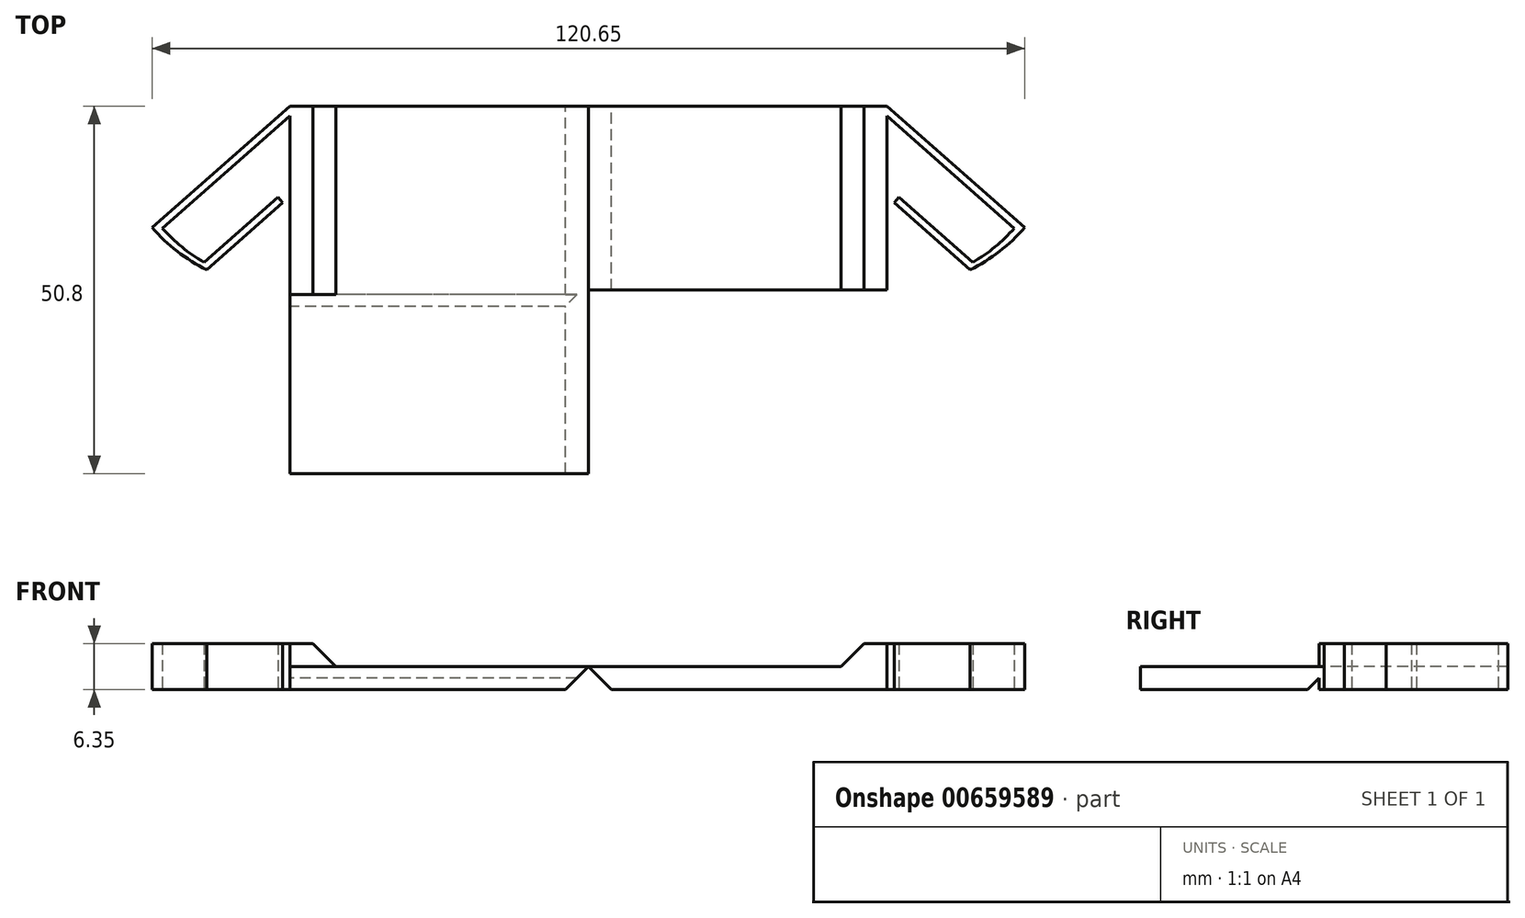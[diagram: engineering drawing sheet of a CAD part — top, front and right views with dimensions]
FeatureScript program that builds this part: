
annotation { "Feature Type Name" : "Feature", "Feature Type Description" : "" }
export const myFeature = defineFeature(function(context is Context, id is Id, definition is map)
    precondition{}
    {
        {
            var Q0;
            Q0=qCreatedBy(makeId("Top.planeOp"),FACE);
            var sketch = newSketch(context, id + "F0", { "sketchPlane" : qUnion([Q0])});
            skLineSegment(sketch, "E0.bottom", {"start": v(28.58, -12.7) * mm, "end": v(-28.58, -12.7) * mm});
            skLineSegment(sketch, "E0.top", {"start": v(28.58, 12.7) * mm, "end": v(-28.58, 12.7) * mm});
            skLineSegment(sketch, "E0.left", {"start": v(28.58, -12.7) * mm, "end": v(28.58, 12.7) * mm});
            skLineSegment(sketch, "E0.right", {"start": v(-28.57, -12.7) * mm, "end": v(-28.57, 12.7) * mm});
            skPoint(sketch, "E0.middle", {"position": v(0, 0) * mm});
            skLineSegment(sketch, "E1", {"start": v(-9.53, 11.37) * mm, "end": v(-9.52, -12.7) * mm});
            skLineSegment(sketch, "E2", {"start": v(0, -12.7) * mm, "end": v(0, 12.7) * mm});
            skPoint(sketch, "E3", {"position": v(-22.22, -12.7) * mm});
            skLineSegment(sketch, "E4", {"start": v(-9.53, 12.7) * mm, "end": v(-28.57, -4.1) * mm});
            skPoint(sketch, "E5", {"position": v(-19.05, -12.7) * mm});
            skArc(sketch, "E6", {"start": v(-28.57, -4.1) * mm, "mid": v(-25.09, -7.37) * mm, "end": v(-21.05, -9.94) * mm});
            skLineSegment(sketch, "E7", {"start": v(-21.05, -9.94) * mm, "end": v(-10.53, -0.66) * mm});
            skLineSegment(sketch, "E8", {"start": v(-10.53, -0.66) * mm, "end": v(-11.19, 0.1) * mm});
            skLineSegment(sketch, "E9", {"start": v(-11.19, 0.1) * mm, "end": v(-11.19, 0.1) * mm});
            skLineSegment(sketch, "E10", {"start": v(-9.53, 11.37) * mm, "end": v(-27.15, -4.18) * mm});
            skArc(sketch, "E11", {"start": v(-27.15, -4.18) * mm, "mid": v(-24.46, -6.77) * mm, "end": v(-21.4, -8.91) * mm});
            skLineSegment(sketch, "E12", {"start": v(-21.4, -8.91) * mm, "end": v(-11.19, 0.1) * mm});
            skSolve(sketch);
        }
        {
            var Q0;
            {var subQ0=sQuery(id+"F0.wireOp",EDGE,"E0.left");Q0=makeQuery(id+"F0.imprint","IMPRINT",FACE,{"disambiguationData":[TD([[makeQuery(id+"F0.imprint","IMPRINT",EDGE,{"derivedFrom":subQ0}),1.0]])]});}
            var Q1;
            {var subQ1=sQuery(id+"F0.wireOp",EDGE,"E1");Q1=makeQuery(id+"F0.imprint","IMPRINT",FACE,{"disambiguationData":[TD([[makeQuery(id+"F0.imprint","IMPRINT",EDGE,{"derivedFrom":subQ1}),1.0]])]});}
            var Q2;
            {var subQ0=sQuery(id+"F0.wireOp",EDGE,"Ll8NUgnO-918t-zldm-zNWz-RsUZQomu35K8");Q2=makeQuery(id+"F0.imprint","IMPRINT",FACE,{"disambiguationData":[TD([[makeQuery(id+"F0.imprint","IMPRINT",EDGE,{"derivedFrom":subQ0}),1.0]])]});}
            extrude(context, id + "F1", {"entities" : qUnion([Q0, Q1, Q2]), "depth" : 3.17 * mm, "offsetDistance" : 25.4 * mm});
        }
        {
            var Q0;
            {var subQ1=sQuery(id+"F0.wireOp",EDGE,"E1");Q0=makeQuery(id+"F0.imprint","IMPRINT",FACE,{"disambiguationData":[TD([[makeQuery(id+"F0.imprint","IMPRINT",EDGE,{"derivedFrom":subQ1}),1.0]])]});}
            extrude(context, id + "F2", {"entities" : qUnion([Q0]), "operationType" : NewBodyOperationType.ADD, "depth" : 6.35 * mm, "offsetDistance" : 25.4 * mm});
        }
        {
            var Q0;
            Q0=makeQuery(id+"F2.opExtrude","CAP_EDGE",EDGE,{"disambiguationData":[OSD([sQuery(id+"F0.wireOp",EDGE,"E2")])],"isStart":false});
            chamfer(context, id + "F3", {"entities" : qUnion([Q0]), "width" : 6.35 * mm, "tangentPropagation" : true});
        }
        {
            var Q0;
            {var subQ0=sQuery(id+"F0.wireOp",EDGE,"E0.left");Q0=makeQuery(id+"F37SAEC6IVc2ddh_1.boolean.opBoolean","MERGE",FACE,{"derivedFrom":[makeQuery(id+"F1.opExtrude","SWEPT_FACE",FACE,{"disambiguationData":[OSD([subQ0])]}),makeQuery(id+"F37SAEC6IVc2ddh_1.opExtrude","SWEPT_FACE",FACE,{"disambiguationData":[OSD([subQ0])]})]});}
            cPlane(context, id + "F4", {"entities" : qUnion([Q0]), "cplaneType" : CPlaneType.OFFSET, "offset" : 3.17 * mm, "width" : 152.4 * mm, "height" : 152.4 * mm});
        }
        {
            var Q0;
            Q0=makeQuery(id+"F1.opExtrude","SWEPT_BODY",BODY,{"disambiguationData":[OSD([sQuery(id+"F0.wireOp",EDGE,"E0.bottom"),sQuery(id+"F0.wireOp",EDGE,"E0.top"),sQuery(id+"F0.wireOp",EDGE,"E0.left"),sQuery(id+"F0.wireOp",EDGE,"E1"),sQuery(id+"F0.wireOp",EDGE,"E4"),sQuery(id+"F0.wireOp",EDGE,"E6"),sQuery(id+"F0.wireOp",EDGE,"E7"),sQuery(id+"F0.wireOp",EDGE,"E8"),sQuery(id+"F0.wireOp",EDGE,"E10"),sQuery(id+"F0.wireOp",EDGE,"E11"),sQuery(id+"F0.wireOp",EDGE,"E12")])]});
            var Q1;
            Q1=qCreatedBy(id+"F4.planeOp",FACE);
            mirror(context, id + "F5", {"entities" : qUnion([Q0]), "mirrorPlane" : qUnion([Q1])});
        }
        {
            var Q0;
            {var subQ0=sQuery(id+"F0.wireOp",EDGE,"E0.bottom");Q0=makeQuery(id+"F2.boolean.opBoolean","MERGE",FACE,{"derivedFrom":[makeQuery(id+"F1.opExtrude","SWEPT_FACE",FACE,{"disambiguationData":[OSD([subQ0])]}),makeQuery(id+"F2.opExtrude","SWEPT_FACE",FACE,{"disambiguationData":[OSD([subQ0])]})]});}
            var sketch = newSketch(context, id + "F6", { "sketchPlane" : qUnion([Q0])});
            skLineSegment(sketch, "E13", {"start": v(28.57, 3.18) * mm, "end": v(31.75, 3.18) * mm});
            skLineSegment(sketch, "E14", {"start": v(31.75, 3.17) * mm, "end": v(28.57, 0) * mm});
            skLineSegment(sketch, "E15", {"start": v(28.57, 0) * mm, "end": v(28.57, 3.18) * mm});
            skLineSegment(sketch, "E16", {"start": v(31.75, 3.18) * mm, "end": v(34.92, 3.18) * mm});
            skLineSegment(sketch, "E17", {"start": v(34.92, 0) * mm, "end": v(31.75, 3.18) * mm});
            skLineSegment(sketch, "E18", {"start": v(34.92, 0) * mm, "end": v(34.92, 3.18) * mm});
            skSolve(sketch);
        }
        {
            var Q0;
            Q0=makeQuery(id+"F6.imprint","IMPRINT",FACE,{"disambiguationData":[TD([[makeQuery(id+"F6.imprint","IMPRINT",EDGE,{"derivedFrom":sQuery(id+"F6.wireOp",EDGE,"E16")}),-1.0]])]});
            var Q1;
            Q1=makeQuery(id+"F6.imprint","IMPRINT",FACE,{"disambiguationData":[TD([[makeQuery(id+"F6.imprint","IMPRINT",EDGE,{"derivedFrom":sQuery(id+"F6.wireOp",EDGE,"E13")}),-1.0]])]});
            var Q2;
            {var subQ0=sQuery(id+"F0.wireOp",EDGE,"E0.bottom");Q2=makeQuery(id+"F5.opPattern","COPY",FACE,{"derivedFrom":makeQuery(id+"F2.boolean.opBoolean","MERGE",FACE,{"derivedFrom":[makeQuery(id+"F1.opExtrude","SWEPT_FACE",FACE,{"disambiguationData":[OSD([subQ0])]}),makeQuery(id+"F2.opExtrude","SWEPT_FACE",FACE,{"disambiguationData":[OSD([subQ0])]})]}),"instanceName":"1"});}
            var Q3;
            Q3=makeQuery(id+"F6.imprint","IMPRINT",FACE,{"disambiguationData":[TD([[makeQuery(id+"F6.imprint","IMPRINT",EDGE,{"derivedFrom":sQuery(id+"F6.wireOp",EDGE,"E15")}),-1.0]])]});
            extrude(context, id + "F7", {"entities" : qUnion([Q0, Q1, Q2, Q3]), "operationType" : NewBodyOperationType.ADD, "oppositeDirection" : true, "depth" : 25.4 * mm, "offsetDistance" : 25.4 * mm});
        }
        {
            var Q0;
            {var subQ0=sQuery(id+"F0.wireOp",EDGE,"E0.bottom");Q0=makeQuery(id+"F7.boolean.opBoolean","MERGE",FACE,{"derivedFrom":[makeQuery(id+"F2.boolean.opBoolean","MERGE",FACE,{"derivedFrom":[makeQuery(id+"F1.opExtrude","SWEPT_FACE",FACE,{"disambiguationData":[OSD([subQ0])]}),makeQuery(id+"F2.opExtrude","SWEPT_FACE",FACE,{"disambiguationData":[OSD([subQ0])]})]}),makeQuery(id+"F7.opExtrude","CAP_FACE",FACE,{"disambiguationData":[OSD([subQ0,sQuery(id+"F0.wireOp",EDGE,"E1"),sQuery(id+"F0.wireOp",EDGE,"E2"),sQuery(id+"F6.wireOp",EDGE,"E13"),sQuery(id+"F6.wireOp",EDGE,"E14")])],"isStart":true})]});}
            extrude(context, id + "F8", {"entities" : qUnion([Q0]), "operationType" : NewBodyOperationType.ADD, "depth" : 25.4 * mm, "offsetDistance" : 25.4 * mm});
        }
        {
            var Q0;
            {var subQ0=sQuery(id+"F0.wireOp",EDGE,"E1");Q0=makeQuery(id+"F8.boolean.opBoolean","MERGE",FACE,{"derivedFrom":[makeQuery(id+"F2.boolean.opBoolean","MERGE",FACE,{"derivedFrom":[makeQuery(id+"F1.opExtrude","SWEPT_FACE",FACE,{"disambiguationData":[OSD([subQ0])]}),makeQuery(id+"F2.opExtrude","SWEPT_FACE",FACE,{"disambiguationData":[OSD([subQ0])]})]}),makeQuery(id+"F8.opExtrude","SWEPT_FACE",FACE,{"disambiguationData":[OSD([sQuery(id+"F0.wireOp",EDGE,"E0.bottom"),subQ0])]})]});}
            var sketch = newSketch(context, id + "F9", { "sketchPlane" : qUnion([Q0])});
            skPoint(sketch, "E19.oppositeSnap0", {"position": v(13.37, 0) * mm});
            skPoint(sketch, "E19.oppositeSnap1", {"position": v(38.1, 3.18) * mm});
            skLineSegment(sketch, "E19.bottom", {"start": v(38.1, 6.35) * mm, "end": v(13.37, 6.35) * mm});
            skLineSegment(sketch, "E19.top", {"start": v(38.1, 3.18) * mm, "end": v(13.37, 3.18) * mm});
            skLineSegment(sketch, "E19.left", {"start": v(38.1, 6.35) * mm, "end": v(38.1, 3.18) * mm});
            skLineSegment(sketch, "E19.right", {"start": v(13.37, 6.35) * mm, "end": v(13.37, 3.18) * mm});
            skSolve(sketch);
        }
        {
            var Q0;
            Q0 = qSketchRegion(id + "F9", true);
            extrude(context, id + "F10", {"entities" : qUnion([Q0]), "operationType" : NewBodyOperationType.REMOVE, "oppositeDirection" : true, "depth" : 25.4 * mm, "offsetDistance" : 25.4 * mm});
        }
        {
            var Q0;
            {var subQ0=sQuery(id+"F0.wireOp",EDGE,"E1");Q0=makeQuery(id+"F8.boolean.opBoolean","MERGE",FACE,{"derivedFrom":[makeQuery(id+"F2.boolean.opBoolean","MERGE",FACE,{"derivedFrom":[makeQuery(id+"F1.opExtrude","SWEPT_FACE",FACE,{"disambiguationData":[OSD([subQ0])]}),makeQuery(id+"F2.opExtrude","SWEPT_FACE",FACE,{"disambiguationData":[OSD([subQ0])]})]}),makeQuery(id+"F8.opExtrude","SWEPT_FACE",FACE,{"disambiguationData":[OSD([sQuery(id+"F0.wireOp",EDGE,"E0.bottom"),subQ0])]})]});}
            var sketch = newSketch(context, id + "F11", { "sketchPlane" : qUnion([Q0])});
            skLineSegment(sketch, "E20", {"start": v(13.37, 0) * mm, "end": v(13.37, 1.59) * mm});
            skPoint(sketch, "E20.endSnap0", {"position": v(13.37, 4.76) * mm});
            skPoint(sketch, "E20.endSnap1", {"position": v(38.1, 1.59) * mm});
            skLineSegment(sketch, "E21", {"start": v(13.37, 1.59) * mm, "end": v(14.97, 0) * mm});
            skLineSegment(sketch, "E22", {"start": v(14.97, 0) * mm, "end": v(13.37, 0) * mm});
            skSolve(sketch);
        }
        {
            var Q0;
            Q0=makeQuery(id+"F11.imprint","IMPRINT",FACE,{"disambiguationData":[TD([[makeQuery(id+"F11.imprint","IMPRINT",EDGE,{"derivedFrom":sQuery(id+"F11.wireOp",EDGE,"E20")}),-1.0]])]});
            extrude(context, id + "F12", {"entities" : qUnion([Q0]), "operationType" : NewBodyOperationType.REMOVE, "oppositeDirection" : true, "depth" : 50.8 * mm, "offsetDistance" : 25.4 * mm});
        }
    });
